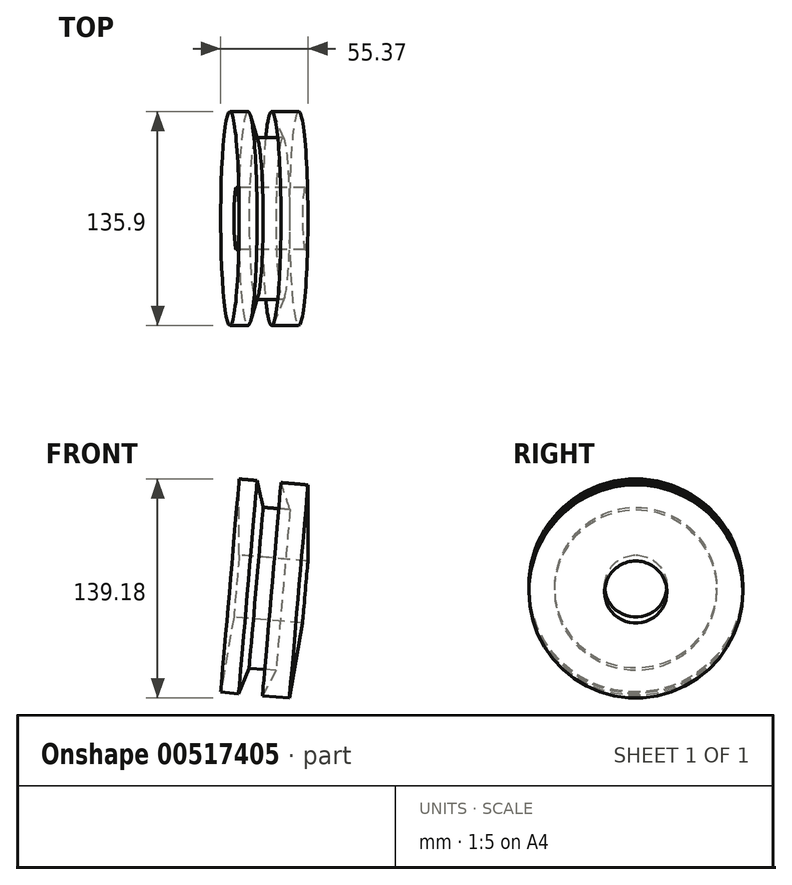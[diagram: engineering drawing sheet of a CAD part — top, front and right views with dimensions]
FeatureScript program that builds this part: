
annotation { "Feature Type Name" : "Feature", "Feature Type Description" : "" }
export const myFeature = defineFeature(function(context is Context, id is Id, definition is map)
    precondition{}
    {
        {
            var Q0;
            Q0=qCreatedBy(makeId("Front.planeOp"),FACE);
            var sketch = newSketch(context, id + "F0", { "sketchPlane" : qUnion([Q0])});
            skLineSegment(sketch, "E0", {"start": v(-32.23, 27.25) * mm, "end": v(-32.23, -21.1) * mm});
            skLineSegment(sketch, "E1", {"start": v(-32.23, -21.1) * mm, "end": v(11.37, -24.88) * mm});
            skLineSegment(sketch, "E2", {"start": v(11.37, -24.88) * mm, "end": v(11.37, 23.46) * mm});
            skLineSegment(sketch, "E3", {"start": v(11.37, 23.46) * mm, "end": v(-5.72, 24.95) * mm});
            skLineSegment(sketch, "E4", {"start": v(-20.86, 26.26) * mm, "end": v(-17.06, 9.24) * mm});
            skLineSegment(sketch, "E5", {"start": v(-17.06, 9.24) * mm, "end": v(0, 7.76) * mm});
            skLineSegment(sketch, "E6", {"start": v(0, 7.76) * mm, "end": v(-5.72, 24.95) * mm});
            skLineSegment(sketch, "E7.trimOffspring", {"start": v(-20.86, 26.26) * mm, "end": v(-32.23, 27.25) * mm});
            skLineSegment(sketch, "E8", {"start": v(-20, -22.15) * mm, "end": v(-21.71, -41.87) * mm, "construction": true});
            skLineSegment(sketch, "E9", {"start": v(-21.71, -41.87) * mm, "end": v(5.65, -44.25) * mm, "construction": true});
            skSolve(sketch);
        }
        {
            var Q0;
            Q0=makeQuery(id+"F0.imprint","IMPRINT",FACE,{"disambiguationData":[TD([[makeQuery(id+"F0.imprint","IMPRINT",EDGE,{"derivedFrom":sQuery(id+"F0.wireOp",EDGE,"E0")}),1.0]])]});
            var Q1;
            Q1=sQuery(id+"F0.wireOp",EDGE,"E9");
            revolve(context, id + "F1", {"entities" : qUnion([Q0]), "axis" : qUnion([Q1]), "revolveType" : RevolveType.FULL});
        }
    });
